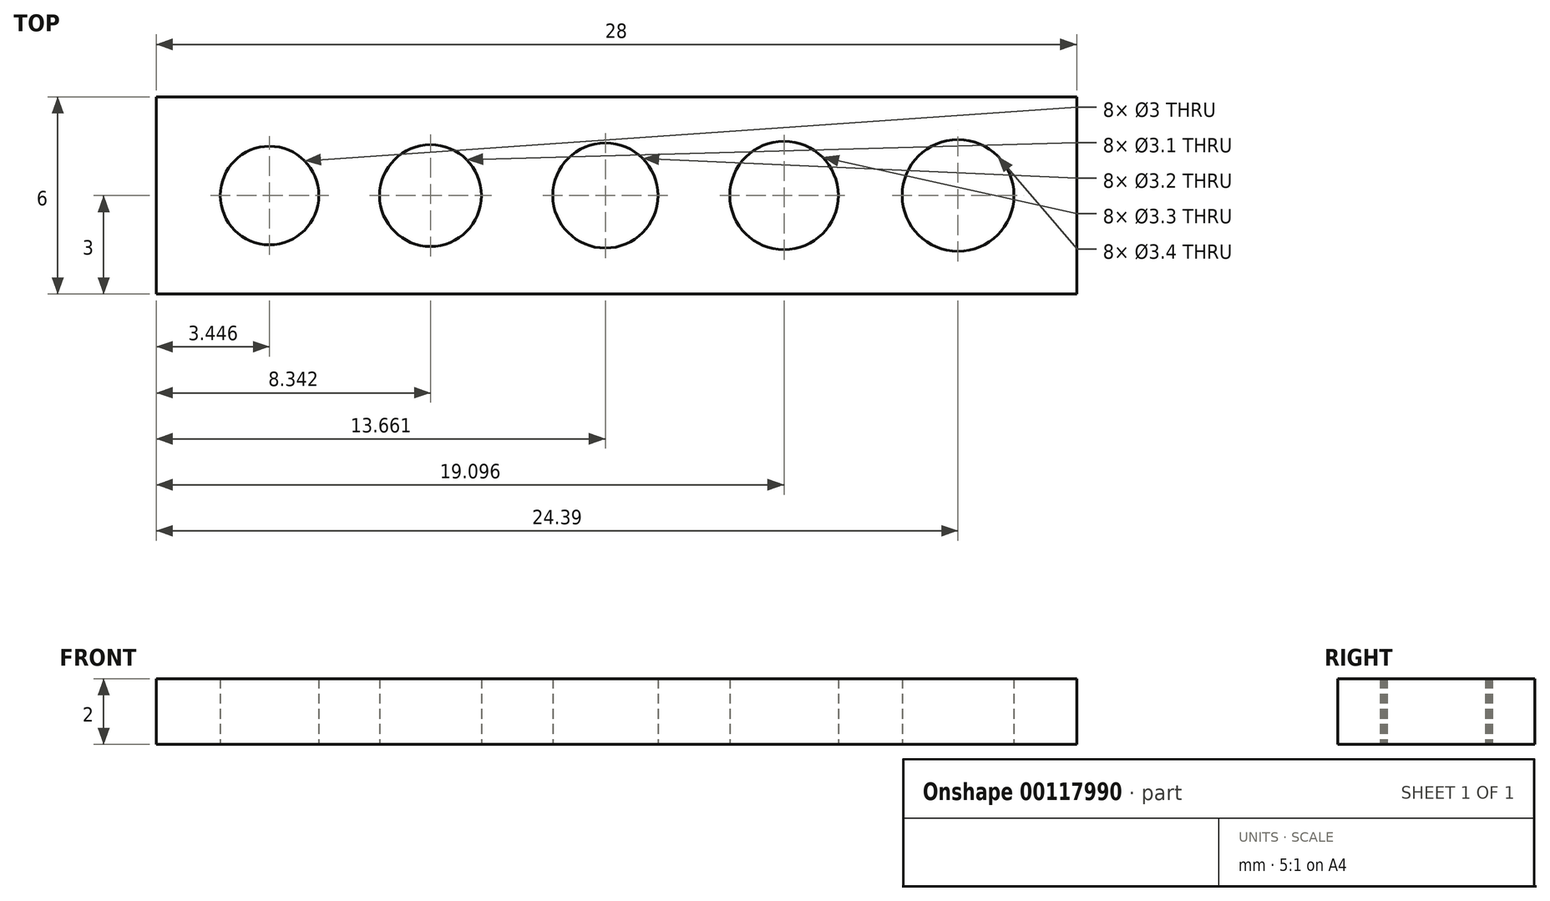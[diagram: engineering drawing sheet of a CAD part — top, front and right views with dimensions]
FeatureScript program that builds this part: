
annotation { "Feature Type Name" : "Feature", "Feature Type Description" : "" }
export const myFeature = defineFeature(function(context is Context, id is Id, definition is map)
    precondition{}
    {
        {
            var Q0;
            Q0=qCreatedBy(makeId("Top.planeOp"),FACE);
            var sketch = newSketch(context, id + "F0", { "sketchPlane" : qUnion([Q0])});
            skLineSegment(sketch, "E0.bottom", {"start": v(-14, 3) * mm, "end": v(14, 3) * mm});
            skLineSegment(sketch, "E0.top", {"start": v(-14, -3) * mm, "end": v(14, -3) * mm});
            skLineSegment(sketch, "E0.left", {"start": v(-14, 3) * mm, "end": v(-14, -3) * mm});
            skLineSegment(sketch, "E0.right", {"start": v(14, 3) * mm, "end": v(14, -3) * mm});
            skLineSegment(sketch, "E1", {"start": v(-14, 0) * mm, "end": v(14, 0) * mm, "construction": true});
            skLineSegment(sketch, "E2", {"start": v(0, 3) * mm, "end": v(0, -3) * mm, "construction": true});
            skCircle(sketch, "E3", {"center": v(-10.55, 0) * mm, "radius": 1.5 * mm});
            skCircle(sketch, "E4", {"center": v(-5.66, 0) * mm, "radius": 1.55 * mm});
            skCircle(sketch, "E5", {"center": v(-0.34, 0) * mm, "radius": 1.6 * mm});
            skCircle(sketch, "E6", {"center": v(5.1, 0) * mm, "radius": 1.65 * mm});
            skCircle(sketch, "E7", {"center": v(10.39, 0) * mm, "radius": 1.7 * mm});
            skSolve(sketch);
        }
        {
            var Q0;
            Q0=makeQuery(id+"F0.imprint","IMPRINT",FACE,{"disambiguationData":[TD([[makeQuery(id+"F0.imprint","IMPRINT",EDGE,{"derivedFrom":sQuery(id+"F0.wireOp",EDGE,"E0.bottom")}),-1.0]])]});
            extrude(context, id + "F1", {"entities" : qUnion([Q0]), "depth" : 2 * mm});
        }
    });
